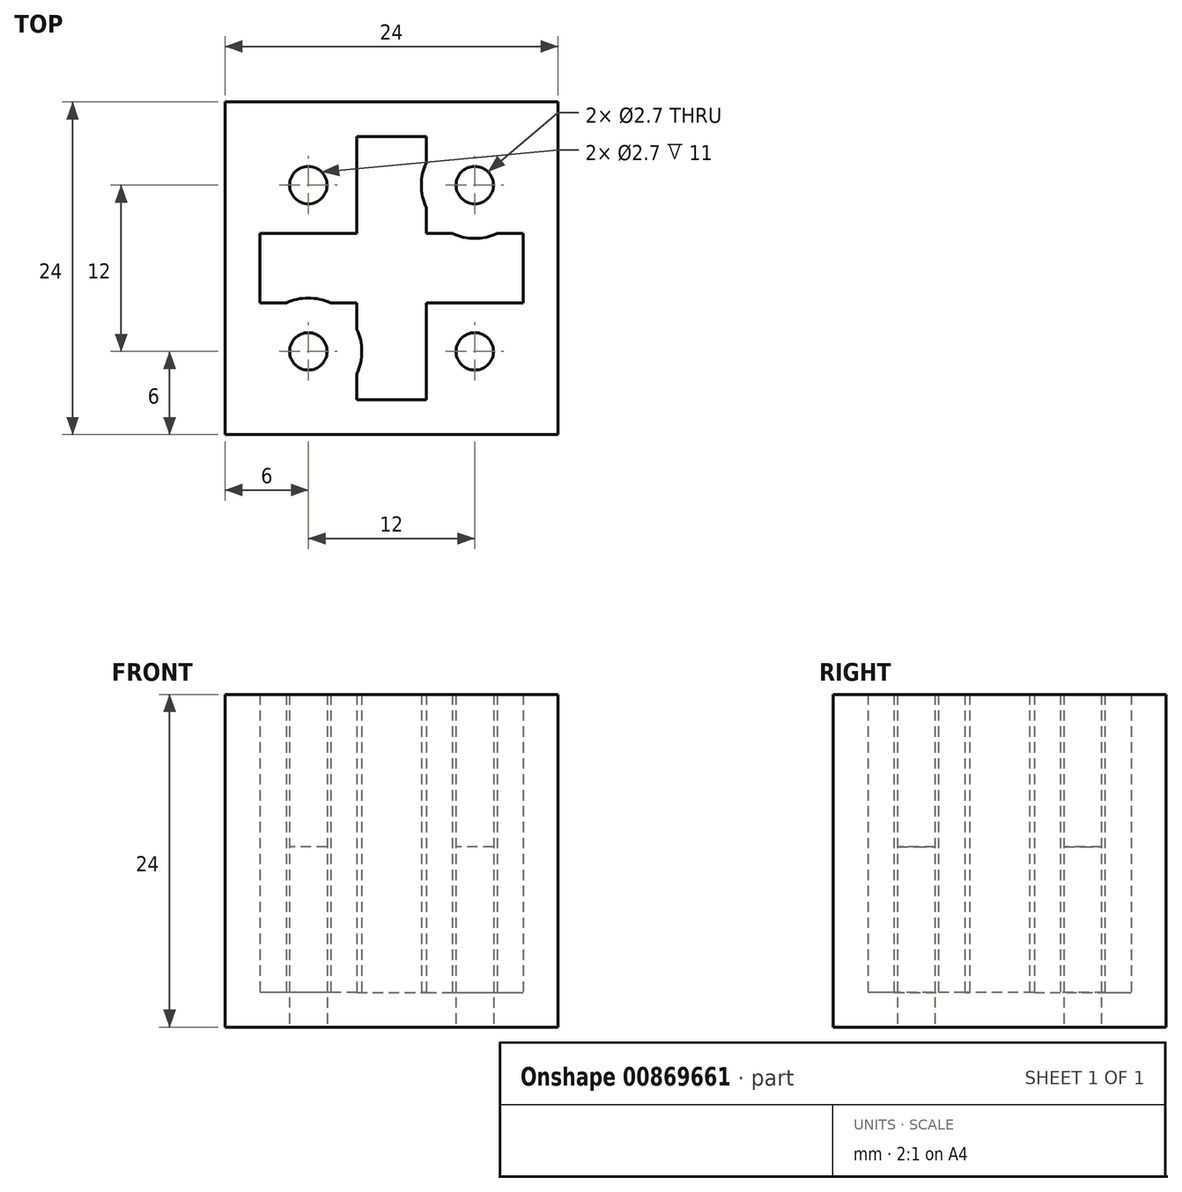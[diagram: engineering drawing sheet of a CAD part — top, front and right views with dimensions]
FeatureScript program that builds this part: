
annotation { "Feature Type Name" : "Feature", "Feature Type Description" : "" }
export const myFeature = defineFeature(function(context is Context, id is Id, definition is map)
    precondition{}
    {
        {
            var Q0;
            Q0=qCreatedBy(makeId("Top.planeOp"),FACE);
            var sketch = newSketch(context, id + "F0", { "sketchPlane" : qUnion([Q0])});
            skLineSegment(sketch, "E0.bottom", {"start": v(-12, 12) * mm, "end": v(12, 12) * mm});
            skLineSegment(sketch, "E0.top", {"start": v(-12, -12) * mm, "end": v(12, -12) * mm});
            skLineSegment(sketch, "E0.left", {"start": v(-12, 12) * mm, "end": v(-12, -12) * mm});
            skLineSegment(sketch, "E0.right", {"start": v(12, 12) * mm, "end": v(12, -12) * mm});
            skPoint(sketch, "E0.middle", {"position": v(0, 0) * mm});
            skLineSegment(sketch, "E1.bottom", {"start": v(-9.5, 9.5) * mm, "end": v(-2.5, 9.5) * mm});
            skLineSegment(sketch, "E1.top", {"start": v(-9.5, 2.5) * mm, "end": v(-2.5, 2.5) * mm});
            skLineSegment(sketch, "E1.left", {"start": v(-9.5, 9.5) * mm, "end": v(-9.5, 2.5) * mm});
            skLineSegment(sketch, "E1.right", {"start": v(-2.5, 9.5) * mm, "end": v(-2.5, 2.5) * mm});
            skLineSegment(sketch, "E2.MirrorCS", {"start": v(-9.5, -2.5) * mm, "end": v(-2.5, -2.5) * mm});
            skLineSegment(sketch, "E3.MirrorCS", {"start": v(-9.5, -9.5) * mm, "end": v(-9.5, -2.5) * mm});
            skLineSegment(sketch, "E4.MirrorCS", {"start": v(-9.5, -9.5) * mm, "end": v(-2.5, -9.5) * mm});
            skLineSegment(sketch, "E5.MirrorCS", {"start": v(-2.5, -9.5) * mm, "end": v(-2.5, -2.5) * mm});
            skLineSegment(sketch, "E6.MirrorCS", {"start": v(9.5, 9.5) * mm, "end": v(2.5, 9.5) * mm});
            skLineSegment(sketch, "E7.MirrorCS", {"start": v(2.5, 9.5) * mm, "end": v(2.5, 2.5) * mm});
            skLineSegment(sketch, "E8.MirrorCS", {"start": v(9.5, 9.5) * mm, "end": v(9.5, 2.5) * mm});
            skLineSegment(sketch, "E9.MirrorCS", {"start": v(9.5, 2.5) * mm, "end": v(2.5, 2.5) * mm});
            skLineSegment(sketch, "E10.MirrorCS", {"start": v(2.5, -9.5) * mm, "end": v(2.5, -2.5) * mm});
            skLineSegment(sketch, "E11.MirrorCS", {"start": v(9.5, -2.5) * mm, "end": v(2.5, -2.5) * mm});
            skLineSegment(sketch, "E12.MirrorCS", {"start": v(9.5, -9.5) * mm, "end": v(9.5, -2.5) * mm});
            skLineSegment(sketch, "E13.MirrorCS", {"start": v(9.5, -9.5) * mm, "end": v(2.5, -9.5) * mm});
            skCircle(sketch, "E14", {"center": v(-6, 6) * mm, "radius": 1.35 * mm});
            skCircle(sketch, "E15.MirrorC", {"center": v(6, 6) * mm, "radius": 1.35 * mm});
            skCircle(sketch, "E16.MirrorC", {"center": v(-6, -6) * mm, "radius": 1.35 * mm});
            skCircle(sketch, "E17.MirrorC", {"center": v(6, -6) * mm, "radius": 1.35 * mm});
            skSolve(sketch);
        }
        {
            var Q0;
            Q0=makeQuery(id+"F0.imprint","IMPRINT",FACE,{"disambiguationData":[TD([[makeQuery(id+"F0.imprint","IMPRINT",EDGE,{"derivedFrom":sQuery(id+"F0.wireOp",EDGE,"E0.bottom")}),-1.0]])]});
            var Q1;
            Q1=makeQuery(id+"F0.imprint","IMPRINT",FACE,{"disambiguationData":[TD([[makeQuery(id+"F0.imprint","IMPRINT",EDGE,{"derivedFrom":sQuery(id+"F0.wireOp",EDGE,"E1.bottom")}),-1.0]])]});
            var Q2;
            Q2=makeQuery(id+"F0.imprint","IMPRINT",FACE,{"disambiguationData":[TD([[makeQuery(id+"F0.imprint","IMPRINT",EDGE,{"derivedFrom":sQuery(id+"F0.wireOp",EDGE,"E14")}),1.0]])]});
            var Q3;
            Q3=makeQuery(id+"F0.imprint","IMPRINT",FACE,{"disambiguationData":[TD([[makeQuery(id+"F0.imprint","IMPRINT",EDGE,{"derivedFrom":sQuery(id+"F0.wireOp",EDGE,"E6.MirrorCS")}),1.0]])]});
            var Q4;
            Q4=makeQuery(id+"F0.imprint","IMPRINT",FACE,{"disambiguationData":[TD([[makeQuery(id+"F0.imprint","IMPRINT",EDGE,{"derivedFrom":sQuery(id+"F0.wireOp",EDGE,"E15.MirrorC")}),-1.0]])]});
            var Q5;
            Q5=makeQuery(id+"F0.imprint","IMPRINT",FACE,{"disambiguationData":[TD([[makeQuery(id+"F0.imprint","IMPRINT",EDGE,{"derivedFrom":sQuery(id+"F0.wireOp",EDGE,"E10.MirrorCS")}),-1.0]])]});
            var Q6;
            Q6=makeQuery(id+"F0.imprint","IMPRINT",FACE,{"disambiguationData":[TD([[makeQuery(id+"F0.imprint","IMPRINT",EDGE,{"derivedFrom":sQuery(id+"F0.wireOp",EDGE,"E17.MirrorC")}),1.0]])]});
            var Q7;
            Q7=makeQuery(id+"F0.imprint","IMPRINT",FACE,{"disambiguationData":[TD([[makeQuery(id+"F0.imprint","IMPRINT",EDGE,{"derivedFrom":sQuery(id+"F0.wireOp",EDGE,"E2.MirrorCS")}),-1.0]])]});
            var Q8;
            Q8=makeQuery(id+"F0.imprint","IMPRINT",FACE,{"disambiguationData":[TD([[makeQuery(id+"F0.imprint","IMPRINT",EDGE,{"derivedFrom":sQuery(id+"F0.wireOp",EDGE,"E16.MirrorC")}),-1.0]])]});
            extrude(context, id + "F1", {"entities" : qUnion([Q0, Q1, Q2, Q3, Q4, Q5, Q6, Q7, Q8]), "depth" : 24 * mm, "offsetDistance" : 25 * mm});
        }
        {
            var Q0;
            Q0=makeQuery(id+"F1.opExtrude","CAP_FACE",FACE,{"disambiguationData":[OSD([sQuery(id+"F0.wireOp",EDGE,"E0.bottom"),sQuery(id+"F0.wireOp",EDGE,"E0.top"),sQuery(id+"F0.wireOp",EDGE,"E0.left"),sQuery(id+"F0.wireOp",EDGE,"E0.right")])],"isStart":false});
            shell(context, id + "F2", {"entities" : qUnion([Q0]), "thickness" : 2.5 * mm});
        }
        {
            var Q0;
            Q0=makeQuery(id+"F0.imprint","IMPRINT",FACE,{"disambiguationData":[TD([[makeQuery(id+"F0.imprint","IMPRINT",EDGE,{"derivedFrom":sQuery(id+"F0.wireOp",EDGE,"E1.bottom")}),-1.0]])]});
            var Q1;
            Q1=makeQuery(id+"F0.imprint","IMPRINT",FACE,{"disambiguationData":[TD([[makeQuery(id+"F0.imprint","IMPRINT",EDGE,{"derivedFrom":sQuery(id+"F0.wireOp",EDGE,"E2.MirrorCS")}),-1.0]])]});
            var Q2;
            Q2=makeQuery(id+"F0.imprint","IMPRINT",FACE,{"disambiguationData":[TD([[makeQuery(id+"F0.imprint","IMPRINT",EDGE,{"derivedFrom":sQuery(id+"F0.wireOp",EDGE,"E10.MirrorCS")}),-1.0]])]});
            var Q3;
            Q3=makeQuery(id+"F0.imprint","IMPRINT",FACE,{"disambiguationData":[TD([[makeQuery(id+"F0.imprint","IMPRINT",EDGE,{"derivedFrom":sQuery(id+"F0.wireOp",EDGE,"E6.MirrorCS")}),1.0]])]});
            extrude(context, id + "F3", {"entities" : qUnion([Q0, Q1, Q2, Q3]), "operationType" : NewBodyOperationType.ADD, "depth" : 24 * mm, "offsetDistance" : 25 * mm});
        }
        {
            var Q0;
            Q0=makeQuery(id+"F0.imprint","IMPRINT",FACE,{"disambiguationData":[TD([[makeQuery(id+"F0.imprint","IMPRINT",EDGE,{"derivedFrom":sQuery(id+"F0.wireOp",EDGE,"E14")}),1.0]])]});
            var Q1;
            Q1=makeQuery(id+"F0.imprint","IMPRINT",FACE,{"disambiguationData":[TD([[makeQuery(id+"F0.imprint","IMPRINT",EDGE,{"derivedFrom":sQuery(id+"F0.wireOp",EDGE,"E16.MirrorC")}),-1.0]])]});
            var Q2;
            Q2=makeQuery(id+"F0.imprint","IMPRINT",FACE,{"disambiguationData":[TD([[makeQuery(id+"F0.imprint","IMPRINT",EDGE,{"derivedFrom":sQuery(id+"F0.wireOp",EDGE,"E17.MirrorC")}),1.0]])]});
            var Q3;
            Q3=makeQuery(id+"F0.imprint","IMPRINT",FACE,{"disambiguationData":[TD([[makeQuery(id+"F0.imprint","IMPRINT",EDGE,{"derivedFrom":sQuery(id+"F0.wireOp",EDGE,"E15.MirrorC")}),-1.0]])]});
            extrude(context, id + "F4", {"entities" : qUnion([Q0, Q1, Q2, Q3]), "operationType" : NewBodyOperationType.ADD, "depth" : 13 * mm, "offsetDistance" : 25 * mm});
        }
    });
